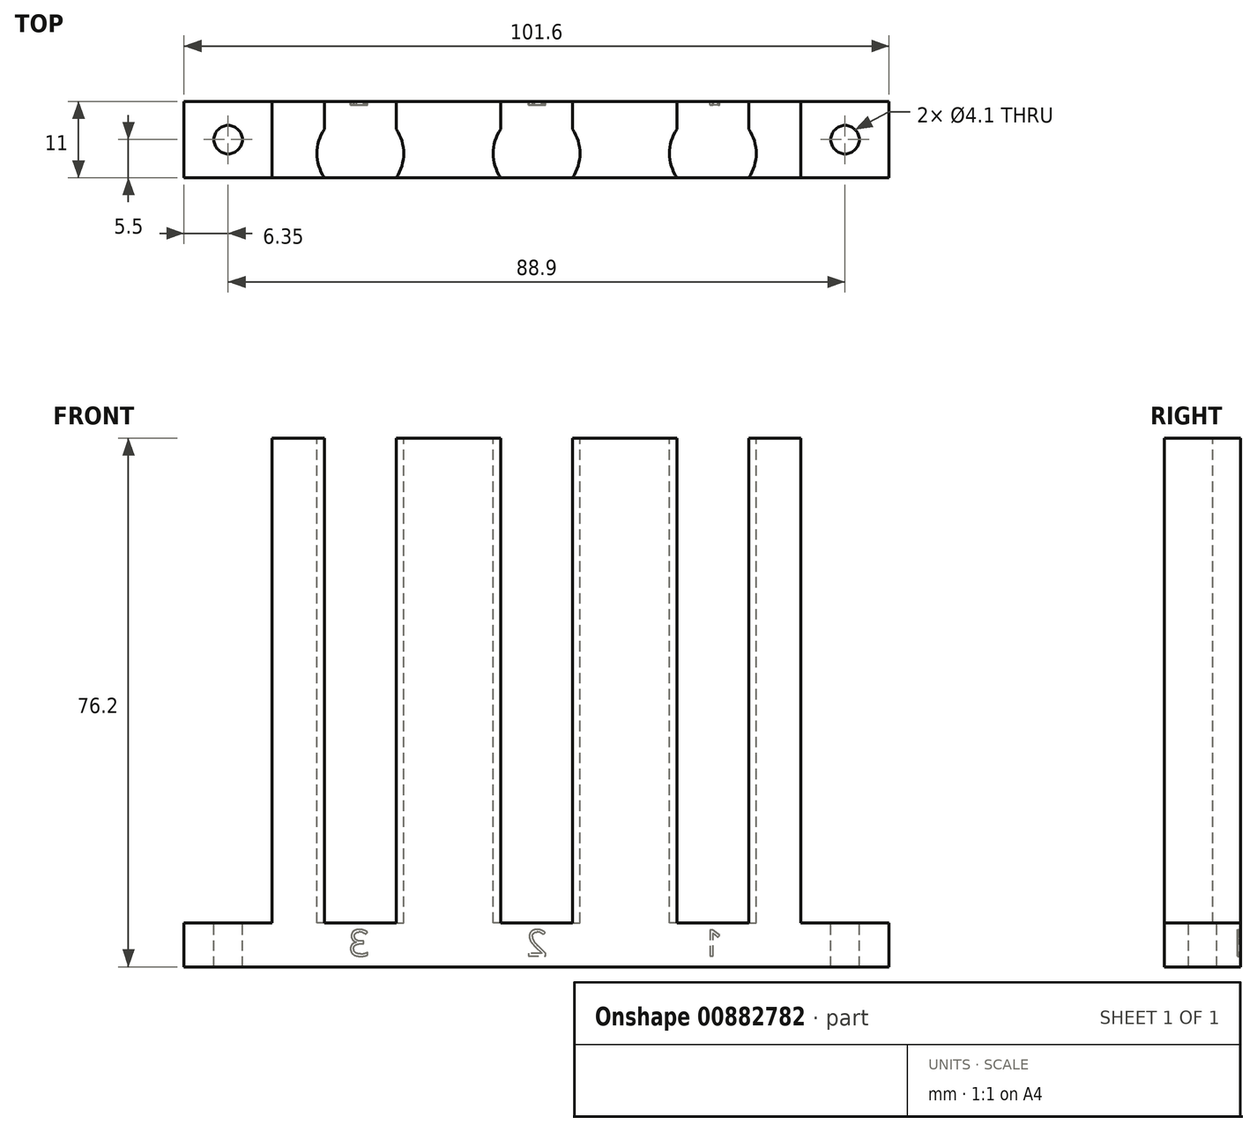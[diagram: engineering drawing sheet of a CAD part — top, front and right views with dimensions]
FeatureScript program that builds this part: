
annotation { "Feature Type Name" : "Feature", "Feature Type Description" : "" }
export const myFeature = defineFeature(function(context is Context, id is Id, definition is map)
    precondition{}
    {
        {
            var Q0;
            Q0=qCreatedBy(makeId("Top.planeOp"),FACE);
            var sketch = newSketch(context, id + "F0", { "sketchPlane" : qUnion([Q0])});
            skLineSegment(sketch, "E0.bottom", {"start": v(38.1, -5.5) * mm, "end": v(-38.1, -5.5) * mm});
            skLineSegment(sketch, "E0.top", {"start": v(38.1, 5.5) * mm, "end": v(-38.1, 5.5) * mm});
            skLineSegment(sketch, "E0.left", {"start": v(38.1, -5.5) * mm, "end": v(38.1, 5.5) * mm});
            skLineSegment(sketch, "E0.right", {"start": v(-38.1, -5.5) * mm, "end": v(-38.1, 5.5) * mm});
            skPoint(sketch, "E0.middle", {"position": v(0, 0) * mm});
            skSolve(sketch);
        }
        {
            var Q0;
            Q0=qSketchRegion(id+"F0",true);
            extrude(context, id + "F1", {"entities" : qUnion([Q0]), "depth" : 76.2 * mm, "offsetDistance" : 25.4 * mm});
        }
        {
            var Q0;
            Q0=makeQuery(id+"F1.opExtrude","CAP_FACE",FACE,{"disambiguationData":[OSD([sQuery(id+"F0.wireOp",EDGE,"E0.bottom"),sQuery(id+"F0.wireOp",EDGE,"E0.top"),sQuery(id+"F0.wireOp",EDGE,"E0.left"),sQuery(id+"F0.wireOp",EDGE,"E0.right")])],"isStart":false});
            var sketch = newSketch(context, id + "F2", { "sketchPlane" : qUnion([Q0])});
            skLineSegment(sketch, "E1", {"start": v(0, 5.5) * mm, "end": v(0, -5.5) * mm});
            skCircle(sketch, "E2", {"center": v(0, -2) * mm, "radius": 6.25 * mm});
            skCircle(sketch, "E3", {"center": v(-25.4, -2) * mm, "radius": 6.25 * mm});
            skCircle(sketch, "E4", {"center": v(25.4, -2) * mm, "radius": 6.25 * mm});
            skSolve(sketch);
        }
        {
            var Q0;
            Q0=qSketchRegion(id+"F2",true);
            extrude(context, id + "F3", {"entities" : qUnion([Q0]), "operationType" : NewBodyOperationType.REMOVE, "oppositeDirection" : true, "depth" : 69.85 * mm, "offsetDistance" : 25.4 * mm});
        }
        {
            var Q0;
            Q0=makeQuery(id+"F1.opExtrude","SWEPT_FACE",FACE,{"disambiguationData":[OSD([sQuery(id+"F0.wireOp",EDGE,"E0.top")])]});
            var sketch = newSketch(context, id + "F4", { "sketchPlane" : qUnion([Q0])});
            skText(sketch, "E5", { "text": "1", "fontName": "OpenSans-Regular.ttf"});
            skText(sketch, "E6", { "text": "2", "fontName": "OpenSans-Regular.ttf"});
            skText(sketch, "E7", { "text": "3", "fontName": "OpenSans-Regular.ttf"});
            const initialGuessF4  = {"E5": [-0.02685, 0.00156, 1, 0, 0.00381], "E6": [-0.00154, 0.00156, 1, 0, 0.00381], "E7": [0.02409, 0.00156, 1, 0, 0.00381]};
            skSetInitialGuess(sketch, initialGuessF4);
            skSolve(sketch);
        }
        {
            var Q0;
            Q0=qSketchRegion(id+"F4",true);
            extrude(context, id + "F5", {"entities" : qUnion([Q0]), "operationType" : NewBodyOperationType.REMOVE, "oppositeDirection" : true, "depth" : 0.5 * mm, "offsetDistance" : 25.4 * mm});
        }
        {
            var Q0;
            Q0=makeQuery(id+"F1.opExtrude","SWEPT_FACE",FACE,{"disambiguationData":[OSD([sQuery(id+"F0.wireOp",EDGE,"E0.left")])]});
            var sketch = newSketch(context, id + "F6", { "sketchPlane" : qUnion([Q0])});
            skLineSegment(sketch, "E8.bottom", {"start": v(-5.5, 0) * mm, "end": v(5.5, 0) * mm});
            skLineSegment(sketch, "E8.top", {"start": v(-5.5, 6.35) * mm, "end": v(5.5, 6.35) * mm});
            skLineSegment(sketch, "E8.left", {"start": v(-5.5, 0) * mm, "end": v(-5.5, 6.35) * mm});
            skLineSegment(sketch, "E8.right", {"start": v(5.5, 0) * mm, "end": v(5.5, 6.35) * mm});
            skSolve(sketch);
        }
        {
            var Q0;
            Q0=qSketchRegion(id+"F6",true);
            extrude(context, id + "F7", {"entities" : qUnion([Q0]), "operationType" : NewBodyOperationType.ADD, "depth" : 12.7 * mm, "offsetDistance" : 25.4 * mm});
        }
        {
            var Q0;
            Q0=makeQuery(id+"F1.opExtrude","SWEPT_FACE",FACE,{"disambiguationData":[OSD([sQuery(id+"F0.wireOp",EDGE,"E0.right")])]});
            var sketch = newSketch(context, id + "F8", { "sketchPlane" : qUnion([Q0])});
            skLineSegment(sketch, "E9.bottom", {"start": v(-5.5, 0) * mm, "end": v(5.5, 0) * mm});
            skLineSegment(sketch, "E9.top", {"start": v(-5.5, 6.35) * mm, "end": v(5.5, 6.35) * mm});
            skLineSegment(sketch, "E9.left", {"start": v(-5.5, 0) * mm, "end": v(-5.5, 6.35) * mm});
            skLineSegment(sketch, "E9.right", {"start": v(5.5, 0) * mm, "end": v(5.5, 6.35) * mm});
            skSolve(sketch);
        }
        {
            var Q0;
            Q0=qSketchRegion(id+"F8",true);
            extrude(context, id + "F9", {"entities" : qUnion([Q0]), "operationType" : NewBodyOperationType.ADD, "depth" : 12.7 * mm, "offsetDistance" : 25.4 * mm});
        }
        {
            var Q0;
            Q0=makeQuery(id+"F9.opExtrude","SWEPT_FACE",FACE,{"disambiguationData":[OSD([sQuery(id+"F8.wireOp",EDGE,"E9.top")])]});
            var sketch = newSketch(context, id + "F10", { "sketchPlane" : qUnion([Q0])});
            skCircle(sketch, "E10", {"center": v(-44.45, 0) * mm, "radius": 2.05 * mm});
            skPoint(sketch, "E11", {"position": v(-38.1, 0) * mm});
            skLineSegment(sketch, "E12", {"start": v(-44.45, 5.5) * mm, "end": v(-44.45, -5.5) * mm});
            skCircle(sketch, "E13.MirrorC", {"center": v(44.45, 0) * mm, "radius": 2.05 * mm});
            skSolve(sketch);
        }
        {
            var Q0;
            Q0=qSketchRegion(id+"F10",true);
            extrude(context, id + "F11", {"entities" : qUnion([Q0]), "operationType" : NewBodyOperationType.REMOVE, "endBound" : BoundingType.UP_TO_NEXT, "oppositeDirection" : true, "depth" : 25.4 * mm, "offsetDistance" : 25.4 * mm});
        }
        {
            var Q0;
            Q0=makeQuery(id+"F1.opExtrude","CAP_FACE",FACE,{"disambiguationData":[OSD([sQuery(id+"F0.wireOp",EDGE,"E0.bottom"),sQuery(id+"F0.wireOp",EDGE,"E0.top"),sQuery(id+"F0.wireOp",EDGE,"E0.left"),sQuery(id+"F0.wireOp",EDGE,"E0.right")])],"isStart":false});
            var sketch = newSketch(context, id + "F12", { "sketchPlane" : qUnion([Q0])});
            skLineSegment(sketch, "E14.bottom", {"start": v(-30.58, 1.5) * mm, "end": v(-20.22, 1.5) * mm});
            skLineSegment(sketch, "E14.top", {"start": v(-30.58, 5.5) * mm, "end": v(-20.22, 5.5) * mm});
            skLineSegment(sketch, "E14.left", {"start": v(-30.58, 1.5) * mm, "end": v(-30.58, 5.5) * mm});
            skLineSegment(sketch, "E14.right", {"start": v(-20.22, 1.5) * mm, "end": v(-20.22, 5.5) * mm});
            skLineSegment(sketch, "E15.bottom", {"start": v(-5.18, 1.5) * mm, "end": v(5.18, 1.5) * mm});
            skLineSegment(sketch, "E15.top", {"start": v(-5.18, 5.5) * mm, "end": v(5.18, 5.5) * mm});
            skLineSegment(sketch, "E15.left", {"start": v(-5.18, 1.5) * mm, "end": v(-5.18, 5.5) * mm});
            skLineSegment(sketch, "E15.right", {"start": v(5.18, 1.5) * mm, "end": v(5.18, 5.5) * mm});
            skLineSegment(sketch, "E16.MirrorCS", {"start": v(30.58, 5.5) * mm, "end": v(20.22, 5.5) * mm});
            skLineSegment(sketch, "E17.MirrorCS", {"start": v(20.22, 1.5) * mm, "end": v(20.22, 5.5) * mm});
            skLineSegment(sketch, "E18.MirrorCS", {"start": v(5.18, 1.5) * mm, "end": v(-5.18, 1.5) * mm});
            skLineSegment(sketch, "E19.MirrorCS", {"start": v(30.58, 1.5) * mm, "end": v(30.58, 5.5) * mm});
            skLineSegment(sketch, "E20.MirrorCS", {"start": v(30.58, 1.5) * mm, "end": v(20.22, 1.5) * mm});
            skLineSegment(sketch, "E21.MirrorCS", {"start": v(5.18, 5.5) * mm, "end": v(-5.18, 5.5) * mm});
            skSolve(sketch);
        }
        {
            var Q0;
            Q0 = qSketchRegion(id + "F12", true);
            var Q1;
            Q1=makeQuery(id+"F9.opExtrude","SWEPT_FACE",FACE,{"disambiguationData":[OSD([sQuery(id+"F8.wireOp",EDGE,"E9.top")])]});
            extrude(context, id + "F13", {"entities" : qUnion([Q0]), "operationType" : NewBodyOperationType.REMOVE, "endBound" : BoundingType.UP_TO_SURFACE, "oppositeDirection" : true, "depth" : 25.4 * mm, "endBoundEntityFace" : qUnion([Q1]), "offsetDistance" : 25.4 * mm});
        }
    });
